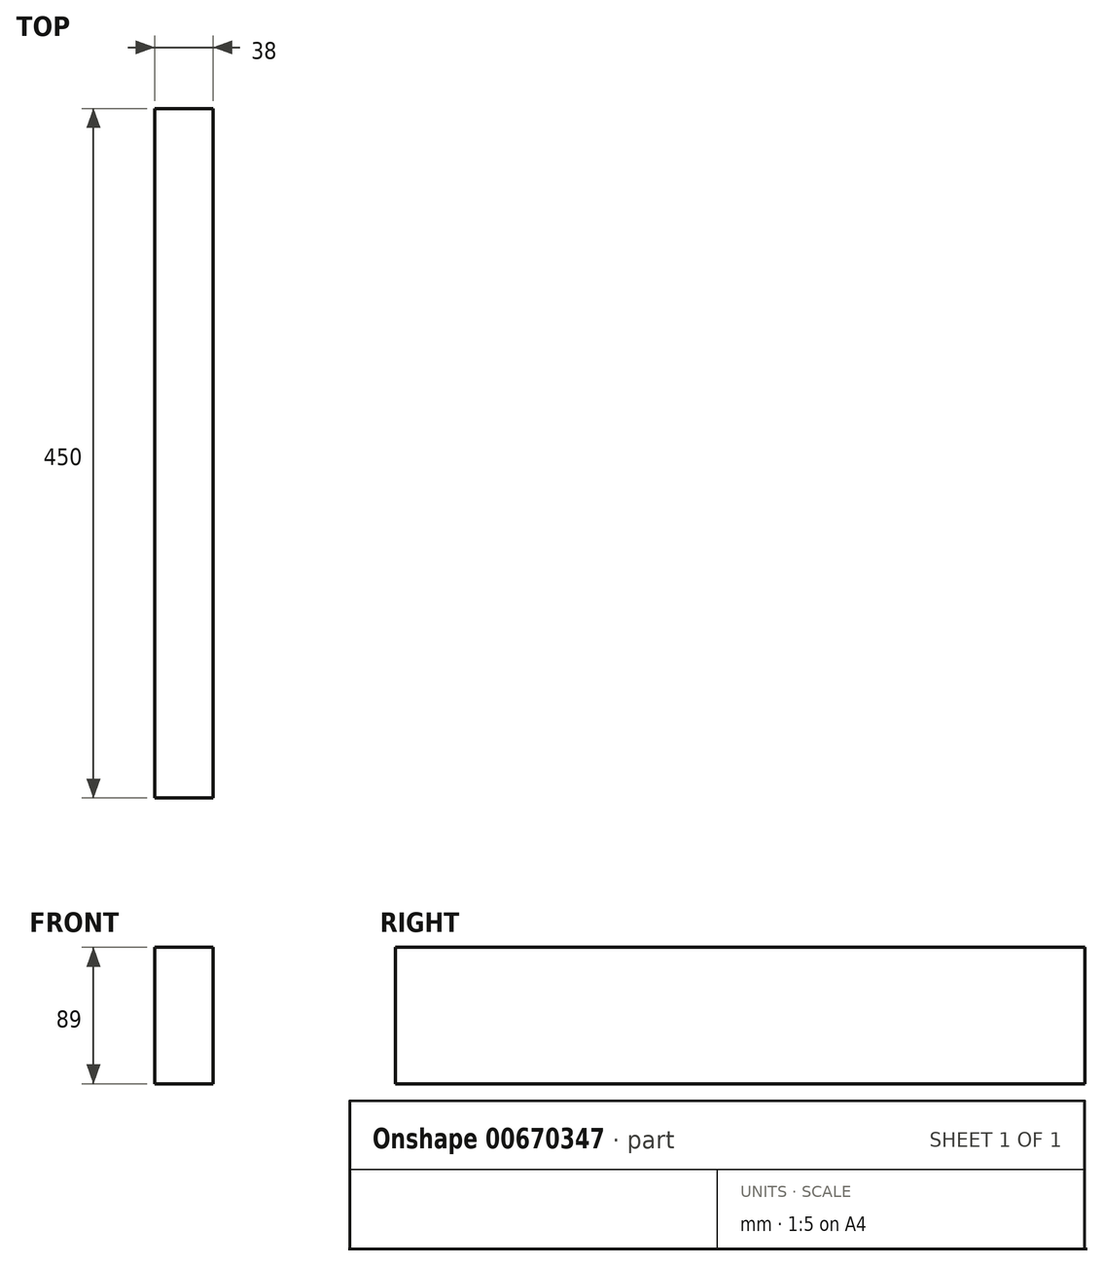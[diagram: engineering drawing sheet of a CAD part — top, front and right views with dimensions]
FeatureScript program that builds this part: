
annotation { "Feature Type Name" : "Feature", "Feature Type Description" : "" }
export const myFeature = defineFeature(function(context is Context, id is Id, definition is map)
    precondition{}
    {
        {
            var Q0;
            Q0=qCreatedBy(makeId("Front.planeOp"),FACE);
            var sketch = newSketch(context, id + "F0", { "sketchPlane" : qUnion([Q0])});
            skLineSegment(sketch, "E0.bottom", {"start": v(-19, 44.5) * mm, "end": v(19, 44.5) * mm});
            skLineSegment(sketch, "E0.top", {"start": v(-19, -44.5) * mm, "end": v(19, -44.5) * mm});
            skLineSegment(sketch, "E0.left", {"start": v(-19, 44.5) * mm, "end": v(-19, -44.5) * mm});
            skLineSegment(sketch, "E0.right", {"start": v(19, 44.5) * mm, "end": v(19, -44.5) * mm});
            skPoint(sketch, "E0.middle", {"position": v(0, 0) * mm});
            skSolve(sketch);
        }
        {
            var Q0;
            Q0 = qSketchRegion(id + "F0", true);
            extrude(context, id + "F1", {"entities" : qUnion([Q0]), "endBound" : BoundingType.SYMMETRIC, "depth" : 450 * mm, "offsetDistance" : 25 * mm});
        }
    });
